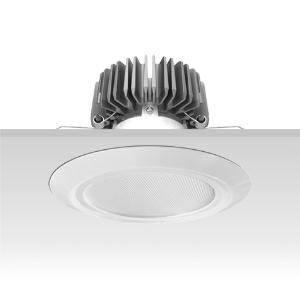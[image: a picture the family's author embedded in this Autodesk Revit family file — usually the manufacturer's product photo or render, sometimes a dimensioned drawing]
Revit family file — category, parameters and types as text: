
# Revit family: 3f_filippi_-_3f_reno_bianco_ampio_3f_filippi_-_30671_a01037_-_3f_reno_200_wh_2000-840_dali_wide___vs_wh_e6d8
name_source: partatom
category: Lighting Fixtures
units: mm (PartAtom-declared; Revit-internal decimal feet)

## family parameters
Cut with Voids When Loaded = No
Host = Face
Light Source = No
Part Type = Normal
Room Calculation Point = No
Round Connector Dimension = Use Diameter
Shared = No

## types (1)
- 3F Filippi - 3F Reno Bianco Ampio (1 x LED, 1723 lm, 20 W, 4000 K)
    Apparent Load = 20 VA
    Approval mark = CE
    CIE Flux Codes = 75 94 99 100 100
    Color Rendering = 80
    Color Temperature = 4000 K
    Control Gear = Electronic transformer
    Default Elevation = 1800 mm
    Description = ILLUMINOTECHNICAL
Luminous efficiency 100% (DLOR 100%, ULOR 0%).
Initial luminous flux of the luminaire 1723 lm.
Direct symmetric wide distribution.
Installation Interdistance Transv.D = 1.16 x hu - Long.D = 1.14 x hu.
Average luminance <3000 cd/m² for radial angles >65°.
Tabular UGR (CIE 117 - 4H-8H; S=0.25H; 70/50/20): RUG 20.4 - 20.3.
Beam angle: 74° - 74°.
Luminous efficacy 86 lm/W.
Lifetime (L90/B10): 30000 h. (tq+25°C)
Lifetime (L85/B10): 50000 h. (tq+25°C)
Lifetime (L70/B10): 80000 h. (tq+25°C)
Sudden decreased luminous flux after 50000 hours: 0% (C0).
Photobiological safety in compliance with IEC/TR 62778: RG0 risk exempt, (IEC 62471).
In compliance with IEC/EN 62722-2-1 - IEC/EN 62717 standards.

SOURCE
Compact LED module 2000/840.
Energy efficiency class (UE 2019/2020 - UE 2019/2015): D.
CIE 13.3 Colour rendering index: CRI >80 (R9 <50%).
IES TM-30 Fidelity Index: Rf = 84 Rg = 95.
CCT nominal colour temperature 4000 K.
Colour initial tolerance (MacAdam): SDCM 3.
Zhaga Book 3 compliant.

MECHANICAL
Passive heat dissipator in die-casting aluminium, oversized, for optimum thermal management of the LED module.
Parabolic element with graduated/concentric rings in white polycarbonate.
Transparent external lens with glossy and satin differentiated surfaces, with a cooling and anti-insect system in methacrylate (PMMA).
Fastening spring clips in stainless steel.
Dimensions: diameter 226 mm, height 146 mm. Weight 1.255 kg.
IP44 protection degree for exposed part, IP20 for recessed part.
Mechanical strength to impacts IK06 (1 joule).
Glow-wire test resistance 650°C.

ELECTRICAL
Wiring on a separate unit.
Halogen Free DALI-2 DATI (Parts 251, 252, 253), PUSH-DIM, electronic wiring 230V-50/60Hz, power factor 0.90 at full load, THD <25%, constant output current, SELV, class II, 1 driver, 1 DALI addresse.
Power of the luminaire 20 W.
ENEC - CE.
SAFE FLICKER: PstLM=<1 and SVM=<0.4 (IEC TR 61547-1 and IEC TR 63158), to ensure a more comfortable and safe light.
Luminaire compliant with EN 60598-2-22 for power supply from a centralised emergency system CPSS (Central Power Supply System), not incorporated in the luminaire - high risk areas excluded. The default power and flux are 100% in AC and 100% in DC.
Ambient temperature from 0°C to +25°C.
Temperature class T6 max 85°C.
Relative humidity UR: <85%.

INSTALLATION
Pull-up recessed fitting.
False ceiling carving: 200 mm.
All accessories dedicated to this product are available on the Catalog and on our website www.3F-Filippi.com.

ACCESSORIES
A01037 - Anti-glare microprismatic VS moulded glass, tempered, not flammable, locked and in line with the trim, in white polycarbonate.

APPLICATIONS
Environments: architectural, commercial, exhibition areas, transit areas, corridors, shops, display windows, service areas.
In false ceilings with narrow voids.

LIGHT MANAGEMENT
Recommended minimum setting: 10%.
The luminaire, equipped with (DALI-2 DATI) driver, can be controlled manually with 3F Easy Dim technology or automatically/manually with wired or wireless DALI/D2D control systems.
The D2D driver guarantees interoperability with other devices with the same certification by making the following information available:
Device Data (Part 251), Energy Report (Part 252), Diagnosis & Maintenance (Part 253).
In electrical systems without a regulation system (manual or automatic) and DALI bus, a suitable jumper must be made on the DA-DA terminals of the appliance.

WARNING
Luminaire designed for disposal/recycling at end-of-life.
Replaceable (LED only) light source by a professional. Replaceable control gear by a professional.
    Height = 0 mm  [stored 0 ft]
    Lamp = 1 x LED
    Lamp Light Flux = 1723 lm
    Lamp Power = 20 W
    Lamp count = 1
    Length = 226 mm
    Lifetime = 50000 h
    Luminous efficacy = 86 lm/W
    Manufacturer = 3F Filippi
    ModVariant = No
    Model = 3F Filippi - 30671+A01037 - 3F Reno 200 WH 2000-840 DALI WIDE + VS WH
    Mounting Place = Ceiling
    Mounting Type = Recessed
    Number of Poles = 1
    OnlyDefault = Yes
    Power Factor = 1
    Product Name = 3F Filippi - 3F Reno Bianco Ampio
    Product group = recessed luminaire
    ProductGroupID = 4
    Protection Class = Protection class II
    Protection Degree = IP 20
    RLX_Detail_Level = 1
    RLX_Emergency_Light_Flux = 0 lm
    RLX_Emergency_Type = 0
    RLX_Emergency_Type_DB = No
    RlxData = <blob elided: 96761 chars, md5=a3b6e7d3>
    Socket = socket
    Standby Power = 0 W
    System Light Flux = 1723 lm
    System Power = 20 W
    Type Comments = Product without accessories
    Type Image = 3ffilippi_3f_reno_200_wh_vs_smp.jpg
    URL = http://relux.com
    VarID = ---
    Voltage = 0 V
    Weight = 0.00 kg
    Width = 0 mm  [stored 0 ft]

note: [stored X ft] marks values corroborated as IEEE doubles in the binary element streams (Revit-internal decimal feet)

## geometry (parser evidence)
native form markers: Blend x4, Sweep x11
no freeform markers — native parametric forms only
